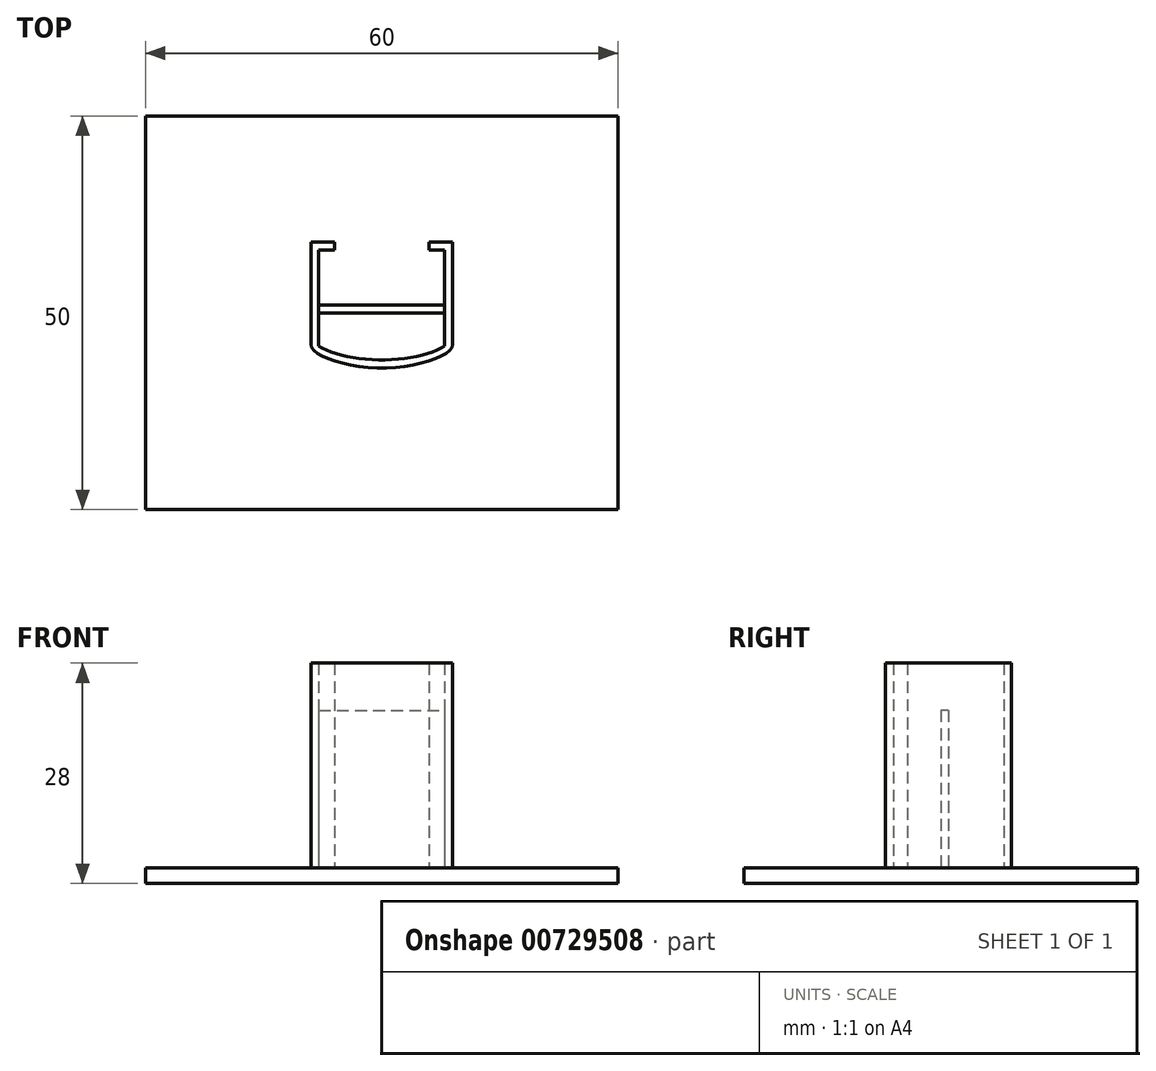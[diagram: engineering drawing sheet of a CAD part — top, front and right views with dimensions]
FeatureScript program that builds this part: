
annotation { "Feature Type Name" : "Feature", "Feature Type Description" : "" }
export const myFeature = defineFeature(function(context is Context, id is Id, definition is map)
    precondition{}
    {
        {
            var Q0;
            Q0=qCreatedBy(makeId("Top.planeOp"),FACE);
            var sketch = newSketch(context, id + "F0", { "sketchPlane" : qUnion([Q0])});
            skLineSegment(sketch, "E0", {"start": v(0, 0) * mm, "end": v(-9, 0) * mm, "construction": true});
            skLineSegment(sketch, "E1", {"start": v(0, 0) * mm, "end": v(9, 0) * mm, "construction": true});
            skLineSegment(sketch, "E2", {"start": v(0, 0) * mm, "end": v(0, 9) * mm, "construction": true});
            skLineSegment(sketch, "E3", {"start": v(0, 0) * mm, "end": v(0, -7) * mm, "construction": true});
            skLineSegment(sketch, "E4", {"start": v(-9, 0) * mm, "end": v(-9, 9) * mm});
            skLineSegment(sketch, "E5", {"start": v(9, 0) * mm, "end": v(9, 9) * mm});
            skLineSegment(sketch, "E6", {"start": v(-9, 9) * mm, "end": v(-6, 9) * mm});
            skLineSegment(sketch, "E7", {"start": v(9, 9) * mm, "end": v(6, 9) * mm});
            skLineSegment(sketch, "E8", {"start": v(-9, 0) * mm, "end": v(-9, -4) * mm});
            skLineSegment(sketch, "E9", {"start": v(9, 0) * mm, "end": v(9, -4) * mm});
            skLineSegment(sketch, "E10", {"start": v(0, 0) * mm, "end": v(0, -1) * mm, "construction": true});
            skFitSpline(sketch, "E11", {"points": [v(-9, -4) * mm, v(0, -7) * mm, v(9, -4) * mm, v(0, -1) * mm, v(-9, -4) * mm]});
            skLineSegment(sketch, "E12", {"start": v(0, 0) * mm, "end": v(0, 0) * mm});
            skLineSegment(sketch, "E13", {"start": v(0, 0) * mm, "end": v(0, -6) * mm, "construction": true});
            skLineSegment(sketch, "E14", {"start": v(-9, 0) * mm, "end": v(-9, -3) * mm, "construction": true});
            skLineSegment(sketch, "E15", {"start": v(9, 0) * mm, "end": v(9, -3) * mm, "construction": true});
            skFitSpline(sketch, "E16", {"points": [v(-9, -3) * mm, v(0, 0) * mm, v(9, -3) * mm, v(0, -6) * mm, v(-9, -3) * mm]});
            skLineSegment(sketch, "E17", {"start": v(-6, 9) * mm, "end": v(-6, 8) * mm});
            skLineSegment(sketch, "E18", {"start": v(6, 9) * mm, "end": v(6, 8) * mm});
            skLineSegment(sketch, "E19", {"start": v(6, 8) * mm, "end": v(8, 8) * mm});
            skLineSegment(sketch, "E20", {"start": v(-6, 8) * mm, "end": v(-8, 8) * mm});
            skLineSegment(sketch, "E21", {"start": v(-8, 8) * mm, "end": v(-8, -4.25) * mm});
            skLineSegment(sketch, "E22", {"start": v(8, 8) * mm, "end": v(8, -4.25) * mm});
            skPoint(sketch, "E23", {"position": v(-8, 0) * mm});
            skLineSegment(sketch, "E24.bottom", {"start": v(-8, 0) * mm, "end": v(8, 0) * mm});
            skLineSegment(sketch, "E24.top", {"start": v(-8, 1) * mm, "end": v(8, 1) * mm});
            skLineSegment(sketch, "E24.left", {"start": v(-8, 0) * mm, "end": v(-8, 1) * mm});
            skLineSegment(sketch, "E24.right", {"start": v(8, 0) * mm, "end": v(8, 1) * mm});
            skSolve(sketch);
        }
        {
            var Q0;
            {var subQ6=sQuery(id+"F0.wireOp",EDGE,"E4");Q0=makeQuery(id+"F0.imprint","IMPRINT",FACE,{"disambiguationData":[TD([[makeQuery(id+"F0.imprint","IMPRINT",EDGE,{"derivedFrom":subQ6}),-1.0]])]});}
            var Q1;
            {var subQ0=sQuery(id+"F0.wireOp",EDGE,"E21");var subQ1=sQuery(id+"F0.wireOp",EDGE,"E11");var subQ2=makeQuery(id+"F0.imprint","INTERSECT",VERTEX,{"derivedFrom":[subQ1,subQ0]});Q1=makeQuery(id+"F0.imprint","IMPRINT",FACE,{"disambiguationData":[TD([[makeQuery(id+"F0.imprint","IMPRINT",EDGE,{"disambiguationData":[TD([[subQ2,-1.0]])],"derivedFrom":subQ1}),-1.0]])]});}
            var Q2;
            {var subQ0=sQuery(id+"F0.wireOp",EDGE,"E11");var subQ1=sQuery(id+"F0.wireOp",EDGE,"E8");var subQ2=makeQuery(id+"F0.imprint","INTERSECT",VERTEX,{"derivedFrom":[subQ1,subQ0]});Q2=makeQuery(id+"F0.imprint","IMPRINT",FACE,{"disambiguationData":[TD([[makeQuery(id+"F0.imprint","IMPRINT",EDGE,{"disambiguationData":[TD([[subQ2,1.0]])],"derivedFrom":subQ1}),1.0]])]});}
            var Q3;
            {var subQ0=sQuery(id+"F0.wireOp",EDGE,"E21");var subQ1=sQuery(id+"F0.wireOp",EDGE,"E11");var subQ2=makeQuery(id+"F0.imprint","INTERSECT",VERTEX,{"derivedFrom":[subQ1,subQ0]});Q3=makeQuery(id+"F0.imprint","IMPRINT",FACE,{"disambiguationData":[TD([[makeQuery(id+"F0.imprint","IMPRINT",EDGE,{"disambiguationData":[TD([[subQ2,-1.0]])],"derivedFrom":subQ1}),1.0]])]});}
            var Q4;
            {var subQ0=sQuery(id+"F0.wireOp",EDGE,"E11");var subQ7=makeQuery(id+"F0.imprint","INTERSECT",VERTEX,{"derivedFrom":[sQuery(id+"F0.wireOp",EDGE,"E8"),subQ0]});Q4=makeQuery(id+"F0.imprint","IMPRINT",FACE,{"disambiguationData":[TD([[makeQuery(id+"F0.imprint","IMPRINT",EDGE,{"disambiguationData":[TD([[subQ7,-1.0]])],"derivedFrom":subQ0}),1.0]])]});}
            var Q5;
            {var subQ0=sQuery(id+"F0.wireOp",EDGE,"E16");var subQ1=sQuery(id+"F0.wireOp",EDGE,"E11");var subQ2=makeQuery(id+"F0.imprint","INTERSECT",VERTEX,{"disambiguationData":[OD(0.0)],"derivedFrom":[subQ1,subQ0]});Q5=makeQuery(id+"F0.imprint","IMPRINT",FACE,{"disambiguationData":[TD([[makeQuery(id+"F0.imprint","IMPRINT",EDGE,{"disambiguationData":[TD([[subQ2,-1.0]])],"derivedFrom":subQ1}),1.0]])]});}
            var Q6;
            {var subQ0=sQuery(id+"F0.wireOp",EDGE,"E16");var subQ1=sQuery(id+"F0.wireOp",EDGE,"E11");var subQ2=makeQuery(id+"F0.imprint","INTERSECT",VERTEX,{"disambiguationData":[OD(0.0)],"derivedFrom":[subQ1,subQ0]});Q6=makeQuery(id+"F0.imprint","IMPRINT",FACE,{"disambiguationData":[TD([[makeQuery(id+"F0.imprint","IMPRINT",EDGE,{"disambiguationData":[TD([[subQ2,-1.0]])],"derivedFrom":subQ1}),-1.0]])]});}
            var Q7;
            {var subQ5=sQuery(id+"F0.wireOp",EDGE,"E5");Q7=makeQuery(id+"F0.imprint","IMPRINT",FACE,{"disambiguationData":[TD([[makeQuery(id+"F0.imprint","IMPRINT",EDGE,{"derivedFrom":subQ5}),1.0]])]});}
            var Q8;
            {var subQ0=sQuery(id+"F0.wireOp",EDGE,"E11");var subQ1=sQuery(id+"F0.wireOp",EDGE,"E9");var subQ2=makeQuery(id+"F0.imprint","INTERSECT",VERTEX,{"derivedFrom":[subQ1,subQ0]});Q8=makeQuery(id+"F0.imprint","IMPRINT",FACE,{"disambiguationData":[TD([[makeQuery(id+"F0.imprint","IMPRINT",EDGE,{"disambiguationData":[TD([[subQ2,1.0]])],"derivedFrom":subQ1}),-1.0]])]});}
            extrude(context, id + "F1", {"entities" : qUnion([Q0, Q1, Q2, Q3, Q4, Q5, Q6, Q7, Q8]), "depth" : 26 * mm, "offsetDistance" : 25 * mm});
        }
        {
            var Q0;
            Q0=qCreatedBy(makeId("Top.planeOp"),FACE);
            var sketch = newSketch(context, id + "F2", { "sketchPlane" : qUnion([Q0])});
            skLineSegment(sketch, "E25.bottom", {"start": v(-30, -25) * mm, "end": v(30, -25) * mm});
            skLineSegment(sketch, "E25.top", {"start": v(-30, 25) * mm, "end": v(30, 25) * mm});
            skLineSegment(sketch, "E25.left", {"start": v(-30, -25) * mm, "end": v(-30, 25) * mm});
            skLineSegment(sketch, "E25.right", {"start": v(30, -25) * mm, "end": v(30, 25) * mm});
            skPoint(sketch, "E26", {"position": v(0, 25) * mm});
            skPoint(sketch, "E27", {"position": v(30, 0) * mm});
            skSolve(sketch);
        }
        {
            var Q0;
            Q0 = qSketchRegion(id + "F2", true);
            extrude(context, id + "F3", {"entities" : qUnion([Q0]), "operationType" : NewBodyOperationType.ADD, "oppositeDirection" : true, "depth" : 2 * mm, "offsetDistance" : 25 * mm});
        }
        {
            var Q0;
            Q0=makeQuery(id+"F0.imprint","IMPRINT",FACE,{"disambiguationData":[TD([[makeQuery(id+"F0.imprint","IMPRINT",EDGE,{"derivedFrom":sQuery(id+"F0.wireOp",EDGE,"E24.top")}),-1.0]])]});
            extrude(context, id + "F4", {"entities" : qUnion([Q0]), "operationType" : NewBodyOperationType.ADD, "depth" : 20 * mm, "offsetDistance" : 25 * mm});
        }
    });
